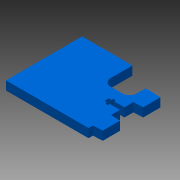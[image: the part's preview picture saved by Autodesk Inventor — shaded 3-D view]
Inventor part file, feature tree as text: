
AUTODESK INVENTOR PART (.ipt)
format: ipt  version: 2013 (Build 170138000, 138)  size: 107,008 bytes
history: native  units: mm
features: extrude x1, sketch x1
ambient origin geometry x8: Origin, YZ Plane, XZ Plane, XY Plane, X Axis, Y Axis, Z Axis, Center Point
bodies: Solid1 (feature_tree)
feature tree (2):
  extrude  "Extrusion1"  [1 undecoded]
  sketch  "Sketch1"  dims[d0=6.0mm d1=0.0mm]
note: 1 required parameter value undecoded (feature->parameter linkage not recoverable at this tier; creation-order binding heuristic only, values carry confidence <= 0.55)
